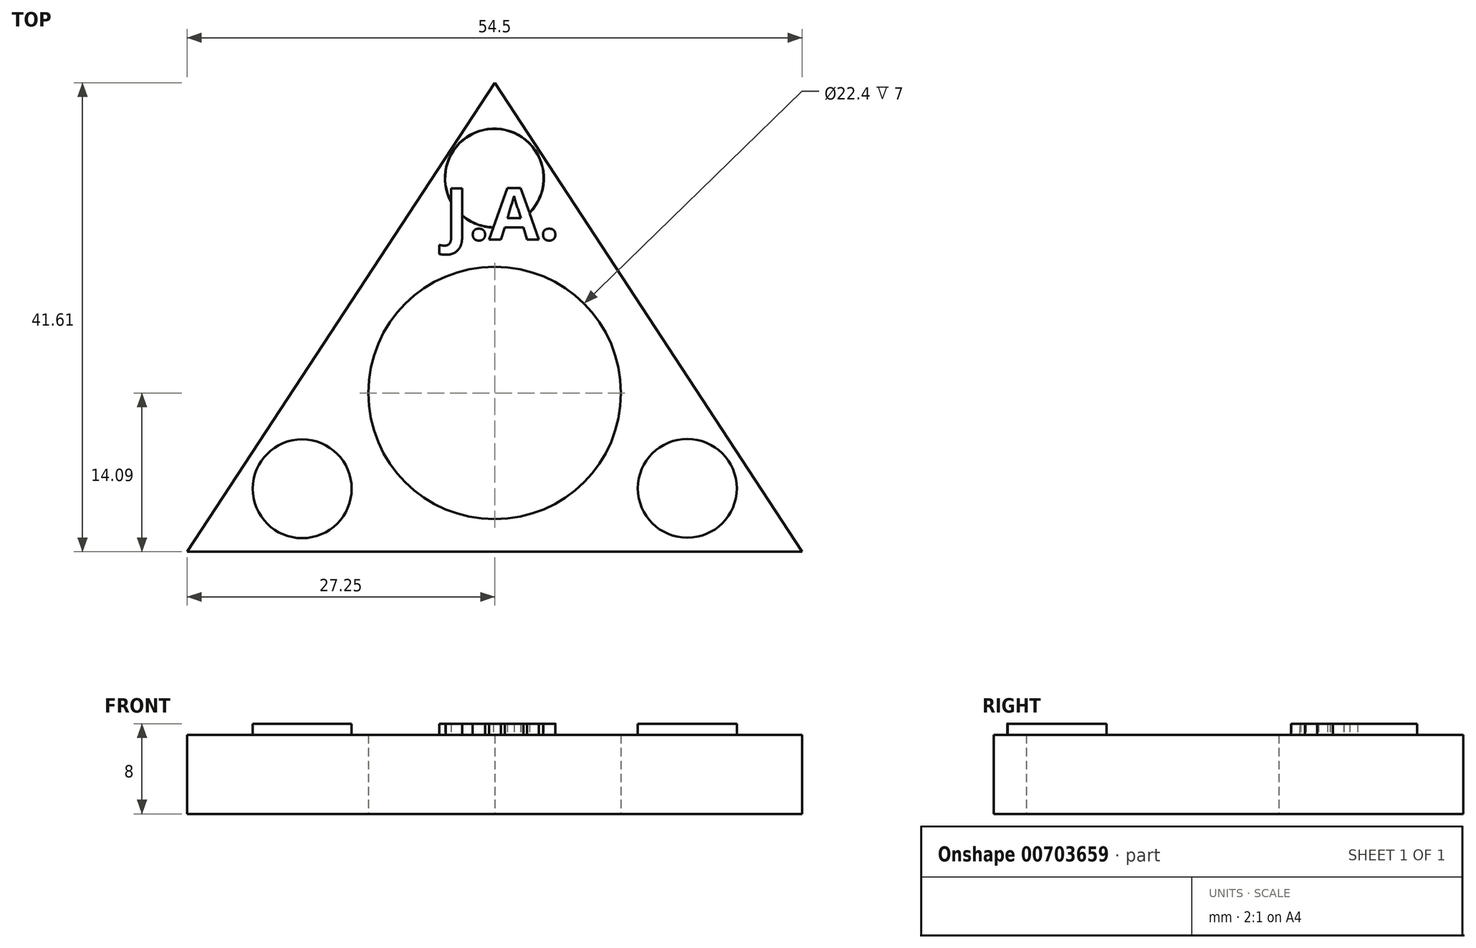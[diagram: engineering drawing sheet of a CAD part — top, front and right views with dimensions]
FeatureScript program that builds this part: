
annotation { "Feature Type Name" : "Feature", "Feature Type Description" : "" }
export const myFeature = defineFeature(function(context is Context, id is Id, definition is map)
    precondition{}
    {
        {
            var Q0;
            Q0=qCreatedBy(makeId("Top.planeOp"),FACE);
            var sketch = newSketch(context, id + "F0", { "sketchPlane" : qUnion([Q0])});
            skCircle(sketch, "E0", {"center": v(0, 0) * mm, "radius": 11.2 * mm});
            skLineSegment(sketch, "E1", {"start": v(0, 27.52) * mm, "end": v(-27.25, -14.1) * mm});
            skLineSegment(sketch, "E2", {"start": v(-27.25, -14.1) * mm, "end": v(27.25, -14.1) * mm});
            skLineSegment(sketch, "E3", {"start": v(27.25, -14.1) * mm, "end": v(0, 27.52) * mm});
            skLineSegment(sketch, "E4.1", {"start": v(21.78, -5.74) * mm, "end": v(21.63, -5.9) * mm});
            skPoint(sketch, "E5.endSnap0", {"position": v(0, -14.1) * mm});
            skLineSegment(sketch, "E6.trimOffspring", {"start": v(21.63, -5.9) * mm, "end": v(21.73, -5.92) * mm, "construction": true});
            skPoint(sketch, "E7.0.midPoint", {"position": v(0, 27.52) * mm});
            skSolve(sketch);
        }
        {
            var Q0;
            Q0 = qSketchRegion(id + "F0", true);
            extrude(context, id + "F1", {"entities" : qUnion([Q0]), "depth" : 7 * mm, "offsetDistance" : 25 * mm});
        }
        {
            var Q0;
            Q0=qCreatedBy(makeId("Top.planeOp"),FACE);
            var sketch = newSketch(context, id + "F2", { "sketchPlane" : qUnion([Q0])});
            skCircle(sketch, "E8", {"center": v(-17.06, -8.5) * mm, "radius": 4.38 * mm});
            skCircle(sketch, "E9.1.0", {"center": v(-0.02, 19.06) * mm, "radius": 4.38 * mm});
            skCircle(sketch, "E9.2.0", {"center": v(17.08, -8.46) * mm, "radius": 4.38 * mm});
            skPoint(sketch, "E9.center", {"position": v(0, 0) * mm});
            skLineSegment(sketch, "E9.anchor1", {"start": v(0, 0) * mm, "end": v(-17.06, -8.5) * mm, "construction": true});
            skLineSegment(sketch, "E9.anchor2", {"start": v(0, 0) * mm, "end": v(17.08, -8.46) * mm, "construction": true});
            skCircle(sketch, "E10", {"center": v(-0.02, 19.06) * mm, "radius": 4.37 * mm});
            skSolve(sketch);
        }
        {
            var Q0;
            Q0 = qSketchRegion(id + "F2", true);
            extrude(context, id + "F3", {"entities" : qUnion([Q0]), "operationType" : NewBodyOperationType.ADD, "depth" : 8 * mm, "offsetDistance" : 25 * mm});
        }
        {
            var Q0;
            Q0=qCreatedBy(makeId("Top.planeOp"),FACE);
            var sketch = newSketch(context, id + "F4", { "sketchPlane" : qUnion([Q0])});
            skText(sketch, "E11", { "text": "J.A.", "fontName": "OpenSans-Bold.ttf"});
            const initialGuessF4  = {"E11": [-0.00442, 0.0136, 1, 0, 0.0046]};
            skSetInitialGuess(sketch, initialGuessF4);
            skSolve(sketch);
        }
        {
            var Q0;
            Q0 = qSketchRegion(id + "F4", true);
            extrude(context, id + "F5", {"entities" : qUnion([Q0]), "operationType" : NewBodyOperationType.ADD, "depth" : 8 * mm, "offsetDistance" : 25 * mm});
        }
        {
            var Q0;
            Q0=sQuery(id+"F0.wireOp",EDGE,"E0");
            extrude(context, id + "F6", {"bodyType" : ToolBodyType.SURFACE, "surfaceEntities" : qUnion([Q0]), "depth" : 7 * mm, "offsetDistance" : 25 * mm});
        }
    });
